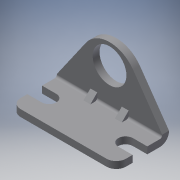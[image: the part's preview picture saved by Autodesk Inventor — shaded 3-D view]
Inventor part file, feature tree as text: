
AUTODESK INVENTOR PART (.ipt)
format: ipt  version: 2018 (Build 220112000, 112)  size: 216,576 bytes
history: native  units: in
note: dims shown in document units (in); Inventor stores cm internally (conversion verified against a paired STEP export)
features: other x126, sketch x9, extrude x8, hole x1
ambient origin geometry x8: Origin, YZ Plane, XZ Plane, XY Plane, X Axis, Y Axis, Z Axis, Center Point
bodies: Solid1 (feature_tree)
feature tree (144):
  extrude  "Extrusion1"  Depth=1.375in TaperAngle=0.0deg
  extrude  "Extrusion2"  Depth=0.375in TaperAngle=0.0deg
  hole  "Hole1"  [1 undecoded]
  extrude  "Extrusion3"  Depth=0.0897in TaperAngle=0.0deg
  extrude  "Extrusion4"  [1 undecoded]
  extrude  "Extrusion5"  [1 undecoded]
  extrude  "Extrusion6"  [1 undecoded]
  extrude  "Extrusion7"  [1 undecoded]
  extrude  "Extrusion8"  [1 undecoded]
  other  "d1_XY"
  other  "d1_YZ"
  other  "d1_ZX"
  other  "d1_X"
  other  "d1_Y"
  other  "d1_Z"
  other  "d1_Center"
  other  "d2_XY"
  other  "d2_YZ"
  other  "d2_ZX"
  other  "d2_X"
  other  "d2_Y"
  other  "d2_Z"
  other  "d2_Center"
  other  "h1_XY"
  other  "h1_YZ"
  other  "h1_ZX"
  other  "h1_X"
  other  "h1_Y"
  other  "h1_Z"
  other  "h1_Center"
  other  "h2_XY"
  other  "h2_YZ"
  other  "h2_ZX"
  other  "h2_X"
  other  "h2_Y"
  other  "h2_Z"
  other  "h2_Center"
  other  "h3_XY"
  other  "h3_YZ"
  other  "h3_ZX"
  other  "h3_X"
  other  "h3_Y"
  other  "h3_Z"
  other  "h3_Center"
  other  "h4_XY"
  other  "h4_YZ"
  other  "h4_ZX"
  other  "h4_X"
  other  "h4_Y"
  other  "h4_Z"
  other  "h4_Center"
  other  "h5_XY"
  other  "h5_YZ"
  other  "h5_ZX"
  other  "h5_X"
  other  "h5_Y"
  other  "h5_Z"
  other  "h5_Center"
  other  "h6_XY"
  other  "h6_YZ"
  other  "h6_ZX"
  other  "h6_X"
  other  "h6_Y"
  other  "h6_Z"
  other  "h6_Center"
  other  "l1_XY"
  other  "l1_YZ"
  other  "l1_ZX"
  other  "l1_X"
  other  "l1_Y"
  other  "l1_Z"
  other  "l1_Center"
  other  "l2_XY"
  other  "l2_YZ"
  other  "l2_ZX"
  other  "l2_X"
  other  "l2_Y"
  other  "l2_Z"
  other  "l2_Center"
  other  "l3_XY"
  other  "l3_YZ"
  other  "l3_ZX"
  other  "l3_X"
  other  "l3_Y"
  other  "l3_Z"
  other  "l3_Center"
  other  "l4_XY"
  other  "l4_YZ"
  other  "l4_ZX"
  other  "l4_X"
  other  "l4_Y"
  other  "l4_Z"
  other  "l4_Center"
  other  "l5_XY"
  other  "l5_YZ"
  other  "l5_ZX"
  other  "l5_X"
  other  "l5_Y"
  other  "l5_Z"
  other  "l5_Center"
  other  "l6_XY"
  other  "l6_YZ"
  other  "l6_ZX"
  other  "l6_X"
  other  "l6_Y"
  other  "l6_Z"
  other  "l6_Center"
  other  "l7_XY"
  other  "l7_YZ"
  other  "l7_ZX"
  other  "l7_X"
  other  "l7_Y"
  other  "l7_Z"
  other  "l7_Center"
  other  "l8_XY"
  other  "l8_YZ"
  other  "l8_ZX"
  other  "l8_X"
  other  "l8_Y"
  other  "l8_Z"
  other  "l8_Center"
  other  "mounting_bracket_XY"
  other  "mounting_bracket_YZ"
  other  "mounting_bracket_ZX"
  other  "mounting_bracket_X"
  other  "mounting_bracket_Y"
  other  "mounting_bracket_Z"
  other  "mounting_bracket_Center"
  other  "mounting_bracket_1_XY"
  other  "mounting_bracket_1_YZ"
  other  "mounting_bracket_1_ZX"
  other  "mounting_bracket_1_X"
  other  "mounting_bracket_1_Y"
  other  "mounting_bracket_1_Z"
  other  "mounting_bracket_1_Center"
  sketch  "Sketch_1"  dims[d0=1.375in d1=0.0in d2=0.1346in d3=0.0in]
  sketch  "Sketch_2"  dims[d4=0.4405in d5=0.75in d6=0.375in d7=0.25in d8=0.5635in d9=0.1346in d10=0.0in d11=0.1346in d12=0.0in]
  sketch  "Sketch3"  dims[d13=0.1346in d14=0.0in d15=0.1346in d16=0.0in]
  sketch  "Sketch_6"  dims[d17=0.1346in d18=0.0in d19=0.0897in d20=0.0in]
  sketch  "Sketch_7"  dims[d21=0.0897in d22=0.0in]
  sketch  "Sketch_8"  dims[d23=0.0in d24=0.0in d25=0.0in d26=0.0in d27=0.0in d28=0.0in d29=0.0in d30=0.0in d31=0.0in]
  sketch  "Sketch_9"
  sketch  "Sketch_10"
  sketch  "Sketch_14"
note: 6 required parameter values undecoded (feature->parameter linkage not recoverable at this tier; creation-order binding heuristic only, values carry confidence <= 0.55)
